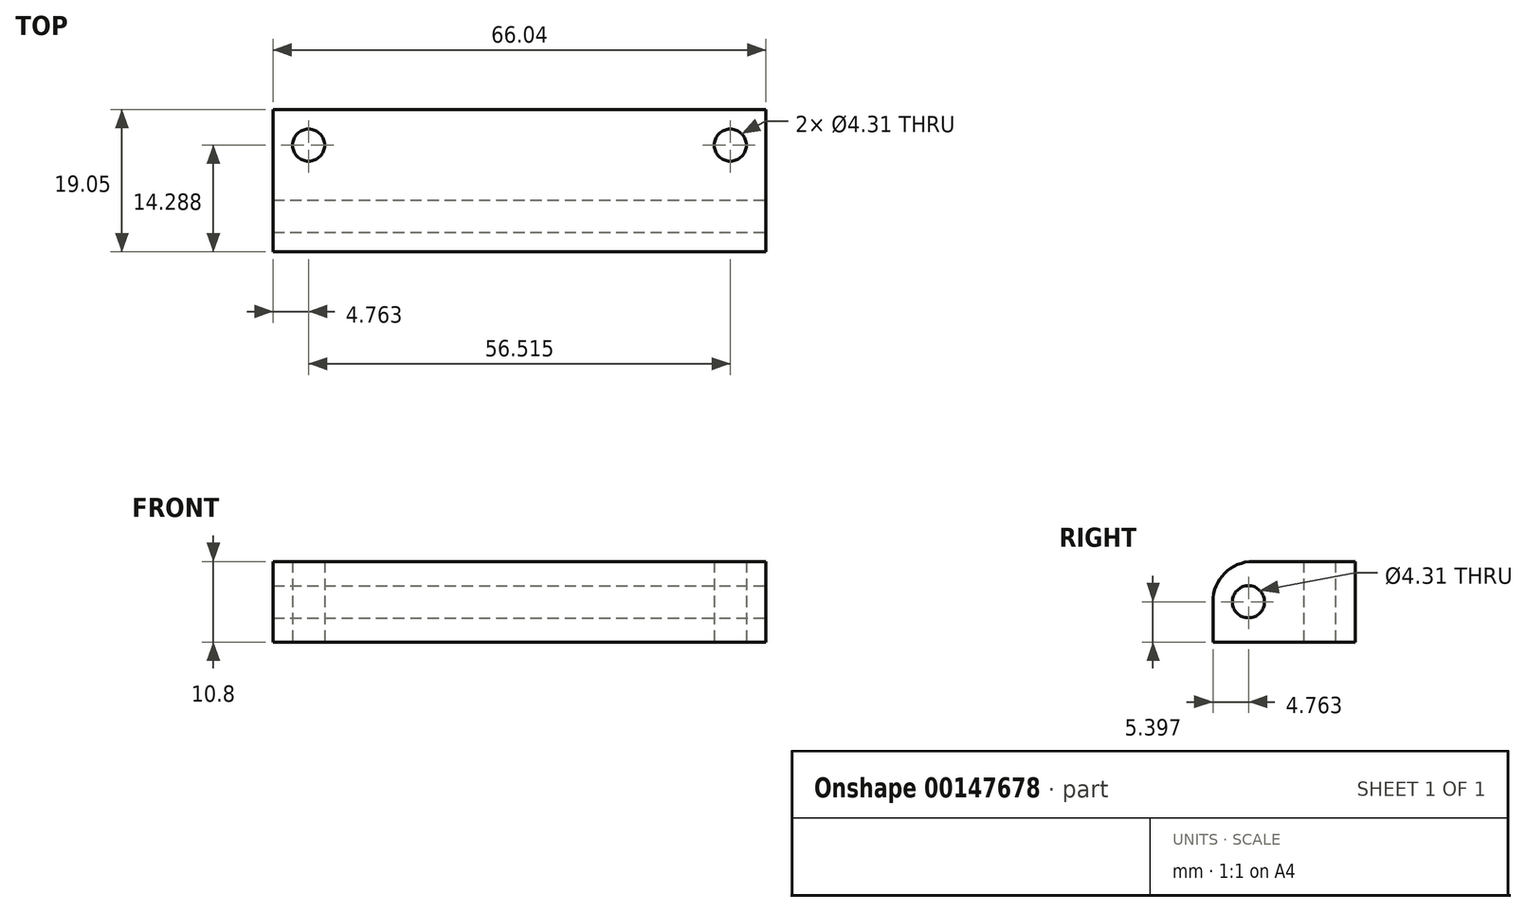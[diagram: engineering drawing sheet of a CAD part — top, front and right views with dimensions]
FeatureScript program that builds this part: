
annotation { "Feature Type Name" : "Feature", "Feature Type Description" : "" }
export const myFeature = defineFeature(function(context is Context, id is Id, definition is map)
    precondition{}
    {
        {
            var Q0;
            Q0=qCreatedBy(makeId("Top.planeOp"),FACE);
            var sketch = newSketch(context, id + "F0", { "sketchPlane" : qUnion([Q0])});
            skLineSegment(sketch, "E0.bottom", {"start": v(0, 0) * mm, "end": v(66.04, 0) * mm});
            skLineSegment(sketch, "E0.top", {"start": v(0, -19.05) * mm, "end": v(66.04, -19.05) * mm});
            skLineSegment(sketch, "E0.left", {"start": v(0, 0) * mm, "end": v(0, -19.05) * mm});
            skLineSegment(sketch, "E0.right", {"start": v(66.04, 0) * mm, "end": v(66.04, -19.05) * mm});
            skLineSegment(sketch, "E1", {"start": v(4.76, 0) * mm, "end": v(4.76, -4.76) * mm, "construction": true});
            skCircle(sketch, "E2", {"center": v(4.76, -4.76) * mm, "radius": 2.15 * mm});
            skLineSegment(sketch, "E3", {"start": v(4.76, -4.76) * mm, "end": v(0, -4.76) * mm, "construction": true});
            skLineSegment(sketch, "E4", {"start": v(66.04, -4.76) * mm, "end": v(61.28, -4.76) * mm, "construction": true});
            skCircle(sketch, "E5", {"center": v(61.28, -4.76) * mm, "radius": 2.15 * mm});
            skSolve(sketch);
        }
        {
            var Q0;
            Q0=qSketchRegion(id+"F0",true);
            extrude(context, id + "F1", {"entities" : qUnion([Q0]), "depth" : 10.8 * mm});
        }
        {
            var Q0;
            Q0=makeQuery(id+"F1.opExtrude","SWEPT_FACE",FACE,{"disambiguationData":[OSD([sQuery(id+"F0.wireOp",EDGE,"E0.right")])]});
            var sketch = newSketch(context, id + "F2", { "sketchPlane" : qUnion([Q0])});
            skLineSegment(sketch, "E6", {"start": v(0, 5.4) * mm, "end": v(-14.29, 5.4) * mm, "construction": true});
            skCircle(sketch, "E7", {"center": v(-14.29, 5.4) * mm, "radius": 2.15 * mm});
            skSolve(sketch);
        }
        {
            var Q0;
            Q0=qSketchRegion(id+"F2",true);
            var Q1;
            Q1=makeQuery(id+"F1.opExtrude","SWEPT_FACE",FACE,{"disambiguationData":[OSD([sQuery(id+"F0.wireOp",EDGE,"E0.left")])]});
            extrude(context, id + "F3", {"entities" : qUnion([Q0]), "operationType" : NewBodyOperationType.REMOVE, "endBound" : BoundingType.UP_TO_SURFACE, "oppositeDirection" : true, "endBoundEntityFace" : qUnion([Q1]), "depth" : 25.4 * mm});
        }
        {
            var Q0;
            Q0=makeQuery(id+"F1.opExtrude","CAP_EDGE",EDGE,{"disambiguationData":[OSD([sQuery(id+"F0.wireOp",EDGE,"E0.top")])],"isStart":false});
            fillet(context, id + "F4", {"entities" : qUnion([Q0]), "radius" : 5.4 * mm, "tangentPropagation" : true, "allowEdgeOverflow" : false});
        }
    });
